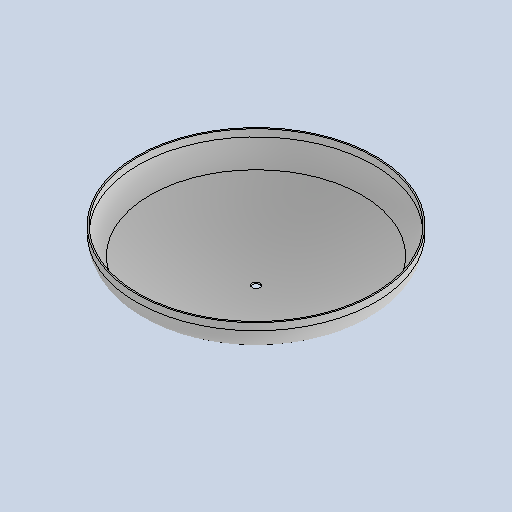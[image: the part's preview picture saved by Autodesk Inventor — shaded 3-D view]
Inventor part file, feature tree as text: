
AUTODESK INVENTOR PART (.ipt)
format: ipt  version: 2025.1 (Build 291241020, 241B)  size: 203,776 bytes
history: native  units: mm
features: sketch x2, revolve x1, extrude x1
ambient origin geometry x8: Origin, YZ Plane, XZ Plane, XY Plane, X Axis, Y Axis, Z Axis, Center Point
bodies: Solid1 (feature_tree)
feature tree (4):
  revolve  "Revolution1"  [1 undecoded]
  extrude  "Extrusion1"  Depth=1000.0mm
  sketch  "Sketch1"  dims[d0=100.0mm d1=30.0mm]
  sketch  "Sketch2"  dims[d3=1000.0mm d6=6.0mm d7=90.0deg d8=33.5mm d9=0.0mm d10=0.0mm d11=1000.0mm d12=226.778984mm]
note: 1 required parameter value undecoded (feature->parameter linkage not recoverable at this tier; creation-order binding heuristic only, values carry confidence <= 0.55)
